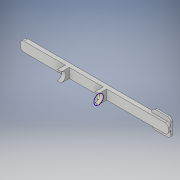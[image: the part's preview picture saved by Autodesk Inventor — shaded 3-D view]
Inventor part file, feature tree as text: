
AUTODESK INVENTOR PART (.ipt)
format: ipt  version: 2018 (Build 220112000, 112)  size: 171,008 bytes
history: native  units: in
note: dims shown in document units (in); Inventor stores cm internally (conversion verified against a paired STEP export)
features: sketch x8, extrude x8, fillet x1
ambient origin geometry x8: Origin, YZ Plane, XZ Plane, XY Plane, X Axis, Y Axis, Z Axis, Center Point
bodies: Solid1 (feature_tree)
feature tree (17):
  sketch  "Sketch1"  dims[d0=5.4in d1=0.15in d2=0.0in]
  extrude  "Extrusion1"  Depth=0.15in TaperAngle=0.0deg
  extrude  "Extrusion2"  Depth=0.15in TaperAngle=0.0deg
  extrude  "Extrusion3"  Depth=0.15in TaperAngle=0.0deg
  extrude  "Extrusion5"  Depth=0.5in TaperAngle=0.0deg
  sketch  "Sketch7"  dims[d26=0.0in d27=0.0in d28=4.7048in]
  extrude  "Extrusion6"  Depth=0.125in TaperAngle=0.0deg
  extrude  "Extrusion7"  Depth=4.7048in
  fillet  "Fillet3"  [1 undecoded]
  extrude  "Extrusion8"  [1 undecoded]
  extrude  "Extrusion9"  [1 undecoded]
  sketch  "Sketch2"  dims[d3=0.35in d4=0.15in d5=0.0in]
  sketch  "Sketch3"  dims[d6=0.15in d7=0.0in d13=0.3in d14=0.0in]
  sketch  "Sketch4"  dims[d19=0.5in d20=0.0in d21=0.5in d22=0.0in]
  sketch  "Sketch6"  dims[d23=0.125in d24=0.2in d25=0.0in]
  sketch  "Sketch8"
  sketch  "Sketch9"
note: 3 required parameter values undecoded (feature->parameter linkage not recoverable at this tier; creation-order binding heuristic only, values carry confidence <= 0.55)
